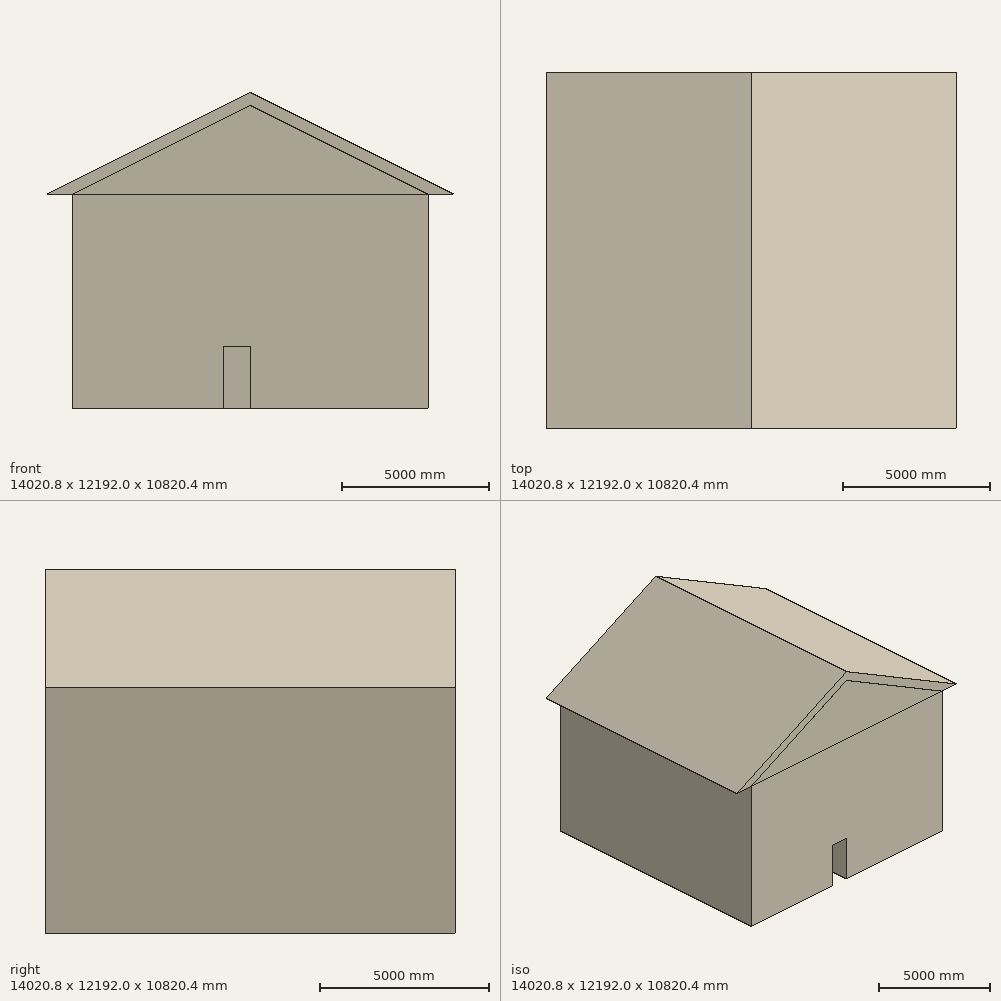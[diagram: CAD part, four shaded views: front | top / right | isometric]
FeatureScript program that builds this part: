
annotation { "Feature Type Name" : "Feature", "Feature Type Description" : "" }
export const myFeature = defineFeature(function(context is Context, id is Id, definition is map)
    precondition{}
    {
        {
            var Q0;
            Q0=qCreatedBy(makeId("Front.planeOp"),FACE);
            var sketch = newSketch(context, id + "F0", { "sketchPlane" : qUnion([Q0])});
            skLineSegment(sketch, "E0", {"start": v(0, 0) * mm, "end": v(-6096, 0) * mm});
            skLineSegment(sketch, "E1", {"start": v(0, 0) * mm, "end": v(6096, 0) * mm});
            skLineSegment(sketch, "E2", {"start": v(0, 0) * mm, "end": v(0, 3048) * mm});
            skLineSegment(sketch, "E3", {"start": v(0, 3048) * mm, "end": v(-6096, 0) * mm});
            skLineSegment(sketch, "E4", {"start": v(0, 3048) * mm, "end": v(6096, 0) * mm});
            skLineSegment(sketch, "E5", {"start": v(0, 3048) * mm, "end": v(0, 3505.2) * mm});
            skLineSegment(sketch, "E6", {"start": v(-6096, 0) * mm, "end": v(-7010.4, 0) * mm});
            skLineSegment(sketch, "E7", {"start": v(6096, 0) * mm, "end": v(7010.4, 0) * mm});
            skLineSegment(sketch, "E8", {"start": v(-7010.4, 0) * mm, "end": v(0, 3505.2) * mm});
            skLineSegment(sketch, "E9", {"start": v(7010.4, 0) * mm, "end": v(0, 3505.2) * mm});
            skLineSegment(sketch, "E10", {"start": v(-6096, 0) * mm, "end": v(-6096, -7315.2) * mm});
            skLineSegment(sketch, "E11", {"start": v(6096, 0) * mm, "end": v(6096, -7315.2) * mm});
            skLineSegment(sketch, "E12", {"start": v(-6096, -7315.2) * mm, "end": v(6096, -7315.2) * mm});
            skLineSegment(sketch, "E13", {"start": v(-914.4, -7315.2) * mm, "end": v(-914.4, -5181.6) * mm});
            skLineSegment(sketch, "E14", {"start": v(-914.4, -5181.6) * mm, "end": v(0, -5181.6) * mm});
            skLineSegment(sketch, "E15", {"start": v(0, -5181.6) * mm, "end": v(0, -7315.2) * mm});
            skLineSegment(sketch, "E16", {"start": v(-914.4, -7315.2) * mm, "end": v(0, -7315.2) * mm});
            skLineSegment(sketch, "E17", {"start": v(-6096, -7315.2) * mm, "end": v(-6096, -7924.8) * mm});
            skLineSegment(sketch, "E18", {"start": v(6096, -7315.2) * mm, "end": v(6096, -7924.8) * mm});
            skLineSegment(sketch, "E19", {"start": v(6096, -7924.8) * mm, "end": v(-6096, -7924.8) * mm});
            skSolve(sketch);
        }
        {
            var Q0;
            Q0=makeQuery(id+"F0.imprint","IMPRINT",FACE,{"disambiguationData":[TD([[makeQuery(id+"F0.imprint","IMPRINT",EDGE,{"derivedFrom":sQuery(id+"F0.wireOp",EDGE,"E3")}),-1.0]])]});
            var Q1;
            Q1=makeQuery(id+"F0.imprint","IMPRINT",FACE,{"disambiguationData":[TD([[makeQuery(id+"F0.imprint","IMPRINT",EDGE,{"derivedFrom":sQuery(id+"F0.wireOp",EDGE,"E4")}),1.0]])]});
            var Q2;
            Q2=makeQuery(id+"F0.imprint","IMPRINT",FACE,{"disambiguationData":[TD([[makeQuery(id+"F0.imprint","IMPRINT",EDGE,{"derivedFrom":sQuery(id+"F0.wireOp",EDGE,"E0")}),1.0]])]});
            extrude(context, id + "F1", {"entities" : qUnion([Q0, Q1, Q2]), "endBound" : BoundingType.SYMMETRIC, "depth" : 12192 * mm, "offsetDistance" : 30.48 * mm});
        }
        {
            var Q0;
            Q0=makeQuery(id+"F0.imprint","IMPRINT",FACE,{"disambiguationData":[TD([[makeQuery(id+"F0.imprint","IMPRINT",EDGE,{"derivedFrom":sQuery(id+"F0.wireOp",EDGE,"E13")}),-1.0]])]});
            extrude(context, id + "F2", {"entities" : qUnion([Q0]), "operationType" : NewBodyOperationType.ADD, "depth" : 30.48 * mm, "offsetDistance" : 30.48 * mm});
        }
        {
            var Q0;
            Q0=makeQuery(id+"F0.imprint","IMPRINT",FACE,{"disambiguationData":[TD([[makeQuery(id+"F0.imprint","IMPRINT",EDGE,{"derivedFrom":sQuery(id+"F0.wireOp",EDGE,"E0")}),-1.0]])]});
            var Q1;
            Q1=makeQuery(id+"F0.imprint","IMPRINT",FACE,{"disambiguationData":[TD([[makeQuery(id+"F0.imprint","IMPRINT",EDGE,{"derivedFrom":sQuery(id+"F0.wireOp",EDGE,"E1")}),1.0]])]});
            extrude(context, id + "F3", {"entities" : qUnion([Q0, Q1]), "endBound" : BoundingType.SYMMETRIC, "depth" : 12192 * mm, "offsetDistance" : 30.48 * mm});
        }
    });
